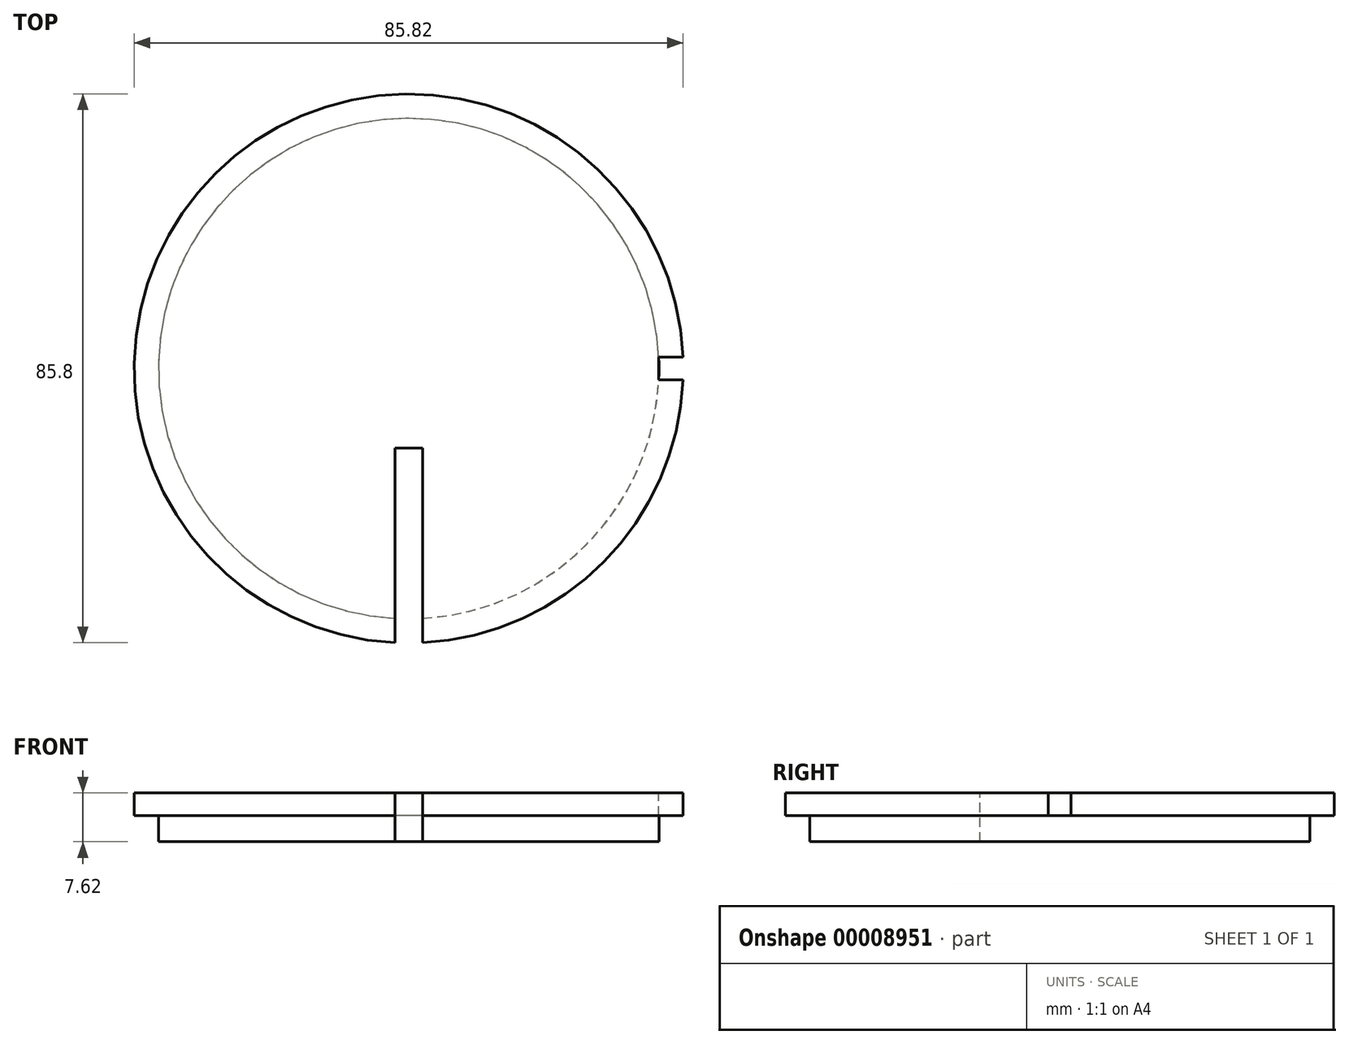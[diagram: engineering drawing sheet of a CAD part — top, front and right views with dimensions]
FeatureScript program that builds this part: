
annotation { "Feature Type Name" : "Feature", "Feature Type Description" : "" }
export const myFeature = defineFeature(function(context is Context, id is Id, definition is map)
    precondition{}
    {
        {
            var Q0;
            Q0=qCreatedBy(makeId("Front.planeOp"),FACE);
            var sketch = newSketch(context, id + "F0", { "sketchPlane" : qUnion([Q0])});
            skLineSegment(sketch, "E0", {"start": v(0, 0) * mm, "end": v(-39.12, 0) * mm});
            skLineSegment(sketch, "E1", {"start": v(-39.12, 0) * mm, "end": v(-39.12, 4.06) * mm});
            skLineSegment(sketch, "E2", {"start": v(-39.12, 4.06) * mm, "end": v(-42.93, 4.06) * mm});
            skLineSegment(sketch, "E3", {"start": v(-42.93, 4.06) * mm, "end": v(-42.93, 7.62) * mm});
            skLineSegment(sketch, "E4", {"start": v(-42.93, 7.62) * mm, "end": v(0, 7.62) * mm});
            skLineSegment(sketch, "E5", {"start": v(0, 7.62) * mm, "end": v(0, 0) * mm});
            skSolve(sketch);
        }
        {
            var Q0;
            Q0=makeQuery(id+"F0.imprint","IMPRINT",FACE,{"disambiguationData":[TD([[makeQuery(id+"F0.imprint","IMPRINT",EDGE,{"derivedFrom":sQuery(id+"F0.wireOp",EDGE,"E0")}),-1.0]])]});
            var Q1;
            Q1=sQuery(id+"F0.wireOp",EDGE,"E5");
            revolve(context, id + "F1", {"entities" : qUnion([Q0]), "axis" : qUnion([Q1]), "revolveType" : RevolveType.FULL});
        }
        {
            var Q0;
            Q0=makeQuery(id+"F1.opRevolve","SWEPT_FACE",FACE,{"disambiguationData":[OSD([sQuery(id+"F0.wireOp",EDGE,"E4")])]});
            var sketch = newSketch(context, id + "F2", { "sketchPlane" : qUnion([Q0])});
            skLineSegment(sketch, "E6", {"start": v(0, 0) * mm, "end": v(42.93, 0) * mm, "construction": true});
            skLineSegment(sketch, "E7", {"start": v(42.89, 1.78) * mm, "end": v(39.08, 1.78) * mm});
            skLineSegment(sketch, "E8", {"start": v(39.08, 1.78) * mm, "end": v(39.08, 0) * mm});
            skLineSegment(sketch, "E9.0.MirrorCS", {"start": v(42.89, -1.78) * mm, "end": v(39.08, -1.78) * mm});
            skLineSegment(sketch, "E10.0.MirrorCS", {"start": v(39.08, -1.78) * mm, "end": v(39.08, 0) * mm});
            skCircle(sketch, "E11.0", {"center": v(0, 0) * mm, "radius": 42.93 * mm});
            skSolve(sketch);
        }
        {
            var Q0;
            {var subQ2=sQuery(id+"F2.wireOp",EDGE,"E7");Q0=makeQuery(id+"F2.imprint","IMPRINT",FACE,{"disambiguationData":[TD([[makeQuery(id+"F2.imprint","IMPRINT",EDGE,{"derivedFrom":subQ2}),1.0]])]});}
            var Q1;
            Q1=makeQuery(id+"F1.opRevolve","SWEPT_FACE",FACE,{"disambiguationData":[OSD([sQuery(id+"F0.wireOp",EDGE,"E2")])]});
            extrude(context, id + "F3", {"entities" : qUnion([Q0]), "operationType" : NewBodyOperationType.REMOVE, "endBound" : BoundingType.UP_TO_SURFACE, "oppositeDirection" : true, "endBoundEntityFace" : qUnion([Q1]), "depth" : 25.4 * mm});
        }
        {
            var Q0;
            Q0=makeQuery(id+"F1.opRevolve","SWEPT_FACE",FACE,{"disambiguationData":[OSD([sQuery(id+"F0.wireOp",EDGE,"E4")])]});
            var sketch = newSketch(context, id + "F4", { "sketchPlane" : qUnion([Q0])});
            skLineSegment(sketch, "E12", {"start": v(0, 0) * mm, "end": v(0, -42.93) * mm, "construction": true});
            skLineSegment(sketch, "E13", {"start": v(2.16, -42.87) * mm, "end": v(2.16, -12.45) * mm});
            skLineSegment(sketch, "E14", {"start": v(2.16, -12.45) * mm, "end": v(0, -12.45) * mm});
            skLineSegment(sketch, "E15.0.MirrorCS", {"start": v(-2.16, -12.45) * mm, "end": v(0, -12.45) * mm});
            skLineSegment(sketch, "E16.0.MirrorCS", {"start": v(-2.16, -42.87) * mm, "end": v(-2.16, -12.45) * mm});
            skArc(sketch, "E17.0", {"start": v(42.89, 1.78) * mm, "mid": v(-42.93, 0) * mm, "end": v(42.89, -1.78) * mm});
            skSolve(sketch);
        }
        {
            var Q0;
            {var subQ2=sQuery(id+"F4.wireOp",EDGE,"E13");Q0=makeQuery(id+"F4.imprint","IMPRINT",FACE,{"disambiguationData":[TD([[makeQuery(id+"F4.imprint","IMPRINT",EDGE,{"derivedFrom":subQ2}),1.0]])]});}
            extrude(context, id + "F5", {"entities" : qUnion([Q0]), "operationType" : NewBodyOperationType.REMOVE, "endBound" : BoundingType.THROUGH_ALL, "oppositeDirection" : true, "depth" : 25.4 * mm});
        }
    });
